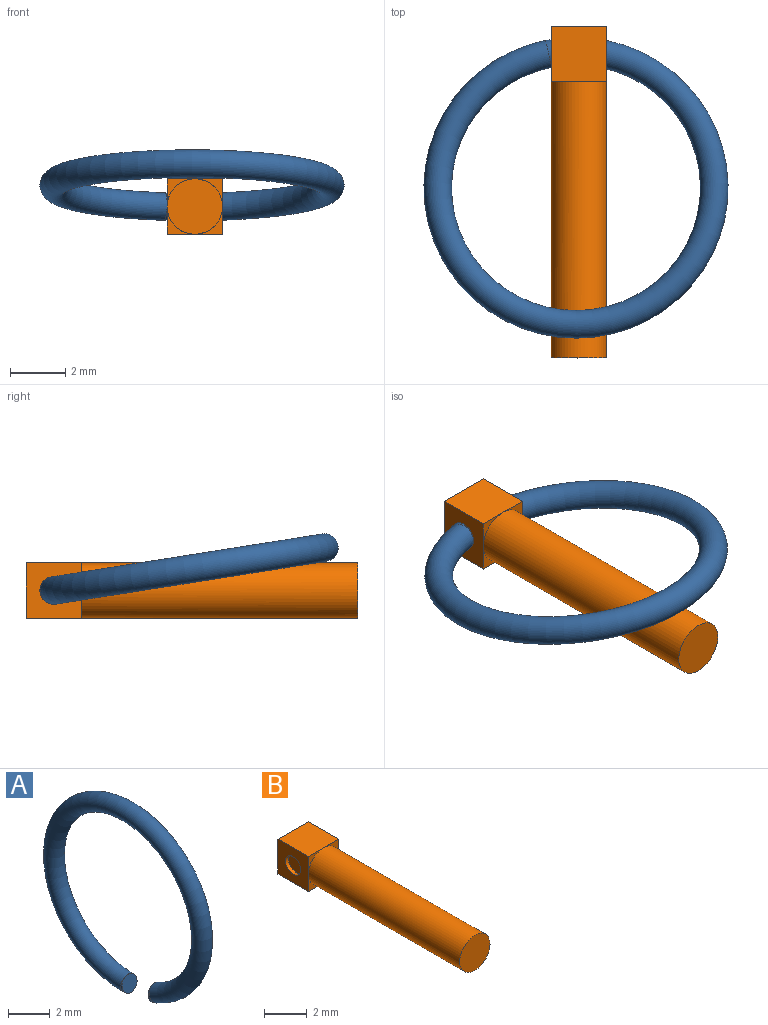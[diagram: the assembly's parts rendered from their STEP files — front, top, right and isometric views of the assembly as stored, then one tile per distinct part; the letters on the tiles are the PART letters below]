
ASSEMBLY  parts=2 mates=1
PART A: 5 faces, bbox 1x11.9x11.9 mm
  f0: torus R=5mm, axis (-1,0,0), area 92.4mm2, adj f1,f3
  f1: torus R=0.5mm, axis (-1,0,0), area 0.3mm2, adj f0,f2
  f2: plane 1x0.98mm, normal (0,0.98,-0.2), area 0.8mm2, adj f1
  f3: torus R=0.5mm, axis (1,0,0), area 0.3mm2, adj f0,f4
  f4: plane 1x0.98mm, normal (0,-0.98,0.2), area 0.8mm2, adj f3
PART B: 15 faces, bbox 2x12x2 mm
  f0: plane 1x1mm, normal (0,-1,0), area 0.2mm2, adj f4,f5,f9
  f1: plane 1x1mm, normal (0,-1,0), area 0.2mm2, adj f5,f6,f9
  f2: plane 1x1mm, normal (0,-1,0), area 0.2mm2, adj f3,f6,f9
  f3: plane 2x2mm, normal (0,0,-1), area 4mm2, adj f2,f4,f6,f7,f8
  f4: plane 2x2mm, normal (1,0,0), area 3.2mm2, adj f0,f3,f5,f7,f8,f11
  f5: plane 2x2mm, normal (0,0,1), area 4mm2, adj f0,f1,f4,f6,f8
  f6: plane 2x2mm, normal (-1,0,0), area 3.2mm2, adj f1,f2,f3,f5,f8,f13
  f7: plane 1x1mm, normal (0,-1,0), area 0.2mm2, adj f3,f4,f9
  f8: plane 2x2mm, normal (0,1,0), area 4mm2, adj f3,f4,f5,f6
  f9: cylinder r=1mm len=10mm, axis (0,1,0), area 62.8mm2, adj f0,f1,f2,f7,f10
  f10: plane 2x2mm, normal (0,-1,0), area 3.1mm2, adj f9
  f11: cylinder r=0.5mm len=1mm, axis (1,0,0), area 0.6mm2, adj f4,f12
  f12: plane 1x1mm, normal (1,0,0), area 0.8mm2, adj f11
  f13: cylinder r=0.5mm len=1mm, axis (-1,0,0), area 0.6mm2, adj f6,f14
  f14: plane 1x1mm, normal (-1,0,0), area 0.8mm2, adj f13
PLACE A rot(axis=(0.59,-0.46,0.67),121.5deg) t=(-1.1,-1.01,0)mm
PLACE B at identity
MATE revolute A.f2 <-> B.f11  axis (-1,0,0) through (0.8,-1,0)mm
